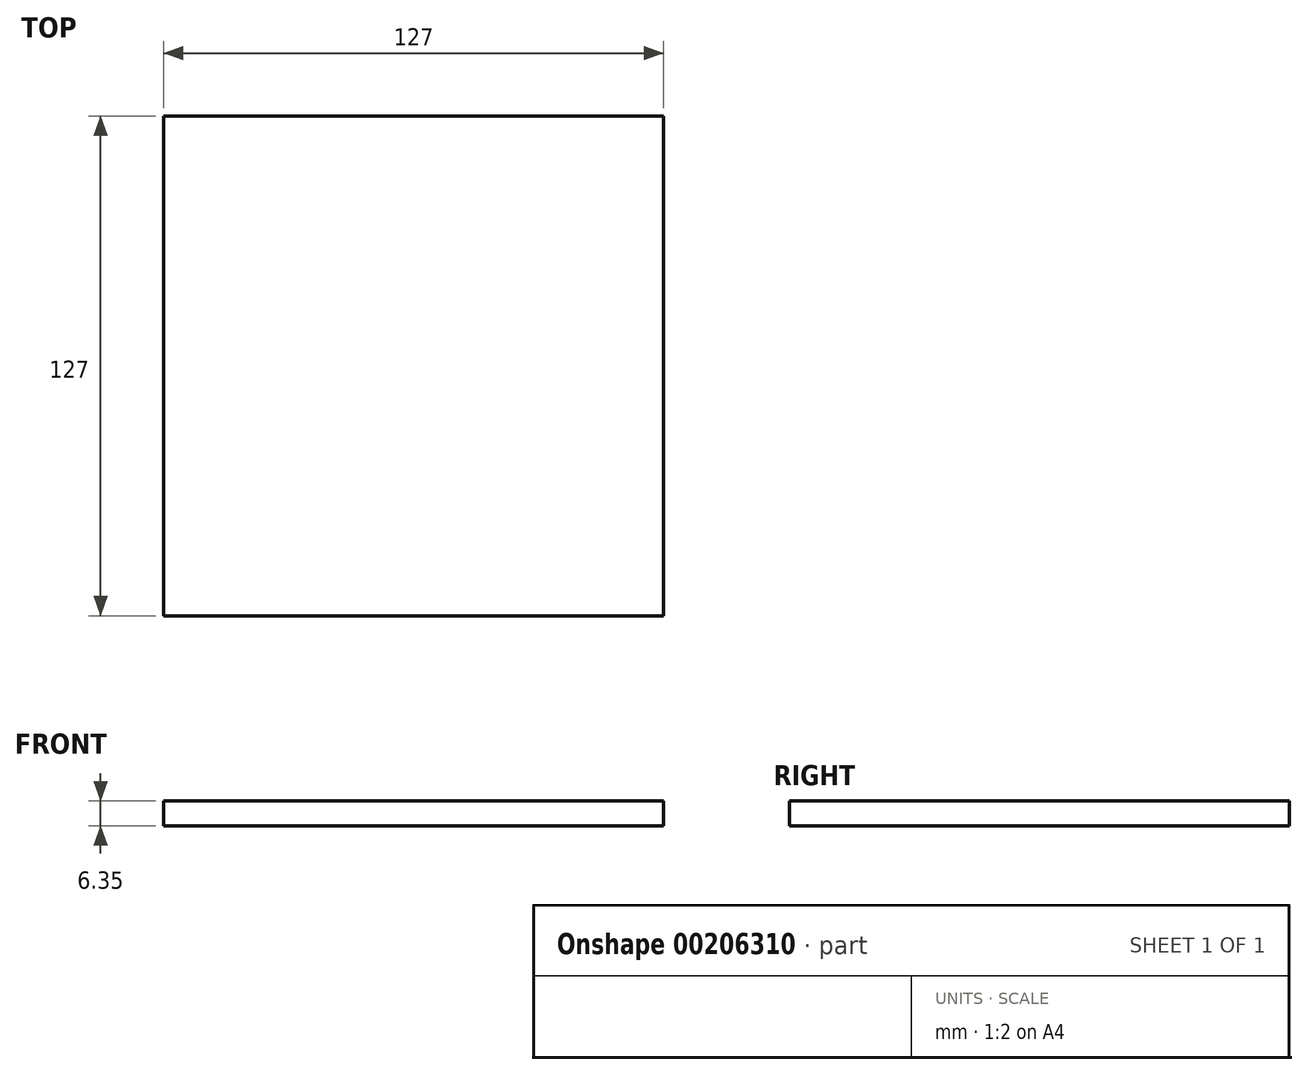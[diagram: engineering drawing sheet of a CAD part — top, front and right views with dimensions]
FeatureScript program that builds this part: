
annotation { "Feature Type Name" : "Feature", "Feature Type Description" : "" }
export const myFeature = defineFeature(function(context is Context, id is Id, definition is map)
    precondition{}
    {
        {
            var Q0;
            Q0=qCreatedBy(makeId("Top.planeOp"),FACE);
            var sketch = newSketch(context, id + "F0", { "sketchPlane" : qUnion([Q0])});
            skLineSegment(sketch, "E0.bottom", {"start": v(0, 0) * mm, "end": v(127, 0) * mm});
            skLineSegment(sketch, "E0.top", {"start": v(0, -127) * mm, "end": v(127, -127) * mm});
            skLineSegment(sketch, "E0.left", {"start": v(0, 0) * mm, "end": v(0, -127) * mm});
            skLineSegment(sketch, "E0.right", {"start": v(127, 0) * mm, "end": v(127, -127) * mm});
            skSolve(sketch);
        }
        {
            var Q0;
            Q0=makeQuery(id+"F0.imprint","IMPRINT",FACE,{"disambiguationData":[TD([[makeQuery(id+"F0.imprint","IMPRINT",EDGE,{"derivedFrom":sQuery(id+"F0.wireOp",EDGE,"E0.bottom")}),-1.0]])]});
            extrude(context, id + "F1", {"entities" : qUnion([Q0]), "depth" : 6.35 * mm});
        }
    });
